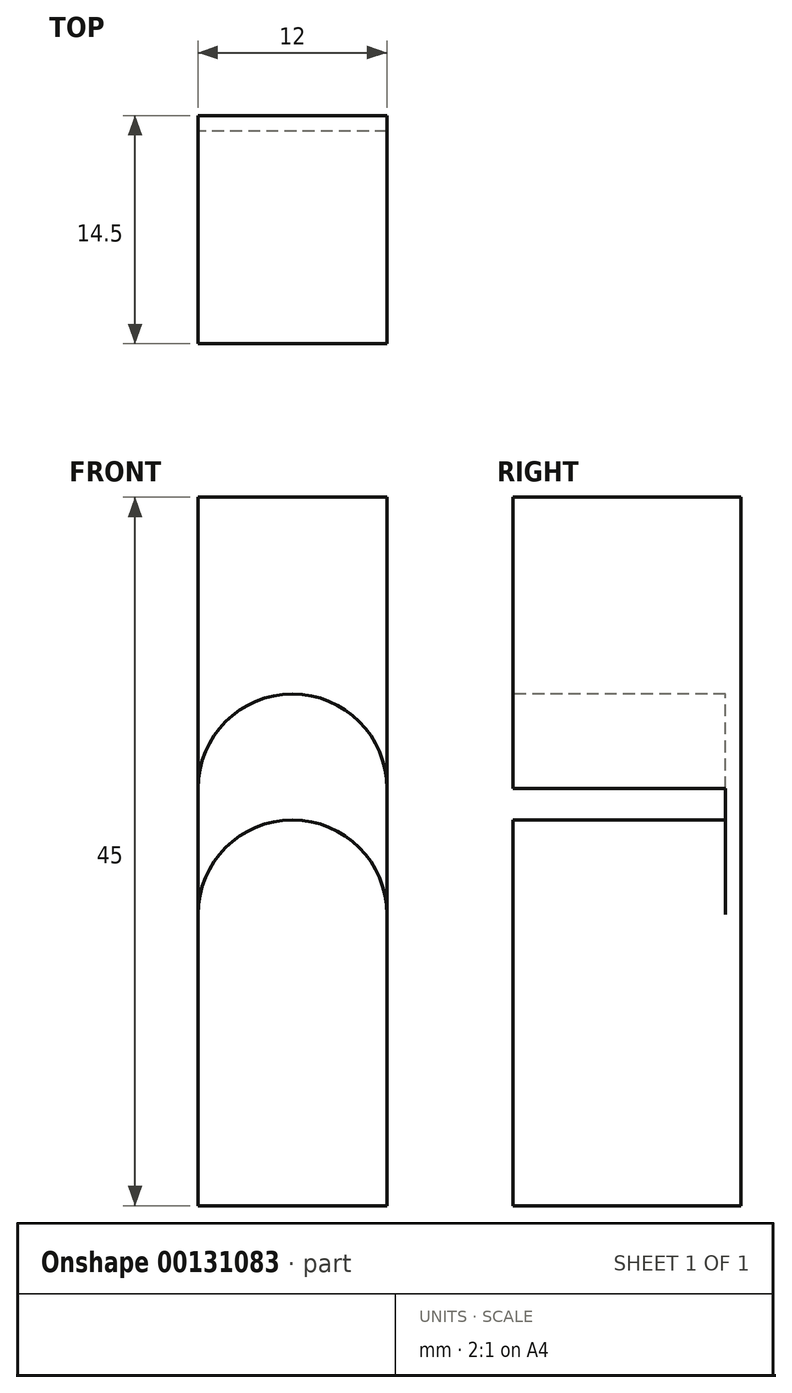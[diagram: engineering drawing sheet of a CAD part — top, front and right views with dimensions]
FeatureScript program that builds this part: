
annotation { "Feature Type Name" : "Feature", "Feature Type Description" : "" }
export const myFeature = defineFeature(function(context is Context, id is Id, definition is map)
    precondition{}
    {
        {
            var Q0;
            Q0=qCreatedBy(makeId("Front.planeOp"),FACE);
            var sketch = newSketch(context, id + "F0", { "sketchPlane" : qUnion([Q0])});
            skLineSegment(sketch, "E0.bottom", {"start": v(-39.38, 79.89) * mm, "end": v(-27.38, 79.89) * mm});
            skLineSegment(sketch, "E0.top", {"start": v(-39.38, 34.89) * mm, "end": v(-27.38, 34.89) * mm});
            skLineSegment(sketch, "E0.left", {"start": v(-39.38, 79.89) * mm, "end": v(-39.38, 34.89) * mm});
            skLineSegment(sketch, "E0.right", {"start": v(-27.38, 79.89) * mm, "end": v(-27.38, 34.89) * mm});
            skSolve(sketch);
        }
        {
            var Q0;
            Q0 = qSketchRegion(id + "F0", true);
            extrude(context, id + "F1", {"entities" : qUnion([Q0]), "depth" : 14.5 * mm});
        }
        {
            var Q0;
            Q0=makeQuery(id+"F1.opExtrude","CAP_FACE",FACE,{"disambiguationData":[OSD([sQuery(id+"F0.wireOp",EDGE,"E0.bottom"),sQuery(id+"F0.wireOp",EDGE,"E0.top"),sQuery(id+"F0.wireOp",EDGE,"E0.left"),sQuery(id+"F0.wireOp",EDGE,"E0.right")])],"isStart":false});
            var sketch = newSketch(context, id + "F2", { "sketchPlane" : qUnion([Q0])});
            skLineSegment(sketch, "E1.bottom", {"start": v(-39.38, 67.39) * mm, "end": v(-27.38, 67.39) * mm});
            skLineSegment(sketch, "E1.top", {"start": v(-39.38, 47.39) * mm, "end": v(-27.38, 47.39) * mm});
            skLineSegment(sketch, "E1.left", {"start": v(-39.38, 67.39) * mm, "end": v(-39.38, 47.39) * mm});
            skLineSegment(sketch, "E1.right", {"start": v(-27.38, 67.39) * mm, "end": v(-27.38, 47.39) * mm});
            skCircle(sketch, "E2", {"center": v(-33.38, 61.39) * mm, "radius": 6 * mm});
            skPoint(sketch, "E2.centerSnap0", {"position": v(-33.38, 67.39) * mm});
            skCircle(sketch, "E3", {"center": v(-33.38, 53.39) * mm, "radius": 6 * mm});
            skPoint(sketch, "E3.centerSnap0", {"position": v(-33.38, 47.39) * mm});
            skSolve(sketch);
        }
        {
            var Q0;
            {var subQ0=sQuery(id+"F2.wireOp",EDGE,"E2");var subQ1=sQuery(id+"F2.wireOp",EDGE,"E1.left");var subQ2=makeQuery(id+"F2.imprint","INTERSECT",VERTEX,{"derivedFrom":[subQ1,subQ0]});Q0=makeQuery(id+"F2.imprint","IMPRINT",FACE,{"disambiguationData":[TD([[makeQuery(id+"F2.imprint","IMPRINT",EDGE,{"disambiguationData":[TD([[subQ2,-1.0]])],"derivedFrom":subQ1}),1.0]])]});}
            var Q1;
            {var subQ0=sQuery(id+"F2.wireOp",EDGE,"E2");var subQ1=sQuery(id+"F2.wireOp",EDGE,"E1.right");var subQ2=makeQuery(id+"F2.imprint","INTERSECT",VERTEX,{"derivedFrom":[subQ1,subQ0]});Q1=makeQuery(id+"F2.imprint","IMPRINT",FACE,{"disambiguationData":[TD([[makeQuery(id+"F2.imprint","IMPRINT",EDGE,{"disambiguationData":[TD([[subQ2,-1.0]])],"derivedFrom":subQ1}),-1.0]])]});}
            var Q2;
            {var subQ0=sQuery(id+"F2.wireOp",EDGE,"E2");var subQ1=makeQuery(id+"F2.imprint","INTERSECT",VERTEX,{"derivedFrom":[sQuery(id+"F2.wireOp",EDGE,"E1.right"),subQ0]});Q2=makeQuery(id+"F2.imprint","IMPRINT",FACE,{"disambiguationData":[TD([[makeQuery(id+"F2.imprint","IMPRINT",EDGE,{"disambiguationData":[TD([[subQ1,-1.0]])],"derivedFrom":subQ0}),1.0]])]});}
            var Q3;
            {var subQ0=sQuery(id+"F2.wireOp",EDGE,"E3");var subQ3=sQuery(id+"F2.wireOp",EDGE,"E2");var subQ4=makeQuery(id+"F2.imprint","INTERSECT",VERTEX,{"disambiguationData":[OD(0.0)],"derivedFrom":[subQ3,subQ0]});Q3=makeQuery(id+"F2.imprint","IMPRINT",FACE,{"disambiguationData":[TD([[makeQuery(id+"F2.imprint","IMPRINT",EDGE,{"disambiguationData":[TD([[subQ4,-1.0]])],"derivedFrom":subQ3}),-1.0]])]});}
            var Q4;
            {var subQ0=sQuery(id+"F2.wireOp",EDGE,"E3");var subQ1=sQuery(id+"F2.wireOp",EDGE,"E2");var subQ2=makeQuery(id+"F2.imprint","INTERSECT",VERTEX,{"disambiguationData":[OD(0.0)],"derivedFrom":[subQ1,subQ0]});Q4=makeQuery(id+"F2.imprint","IMPRINT",FACE,{"disambiguationData":[TD([[makeQuery(id+"F2.imprint","IMPRINT",EDGE,{"disambiguationData":[TD([[subQ2,-1.0]])],"derivedFrom":subQ1}),1.0]])]});}
            extrude(context, id + "F3", {"entities" : qUnion([Q0, Q1, Q2, Q3, Q4]), "operationType" : NewBodyOperationType.REMOVE, "oppositeDirection" : true, "depth" : 13.5 * mm});
        }
    });
